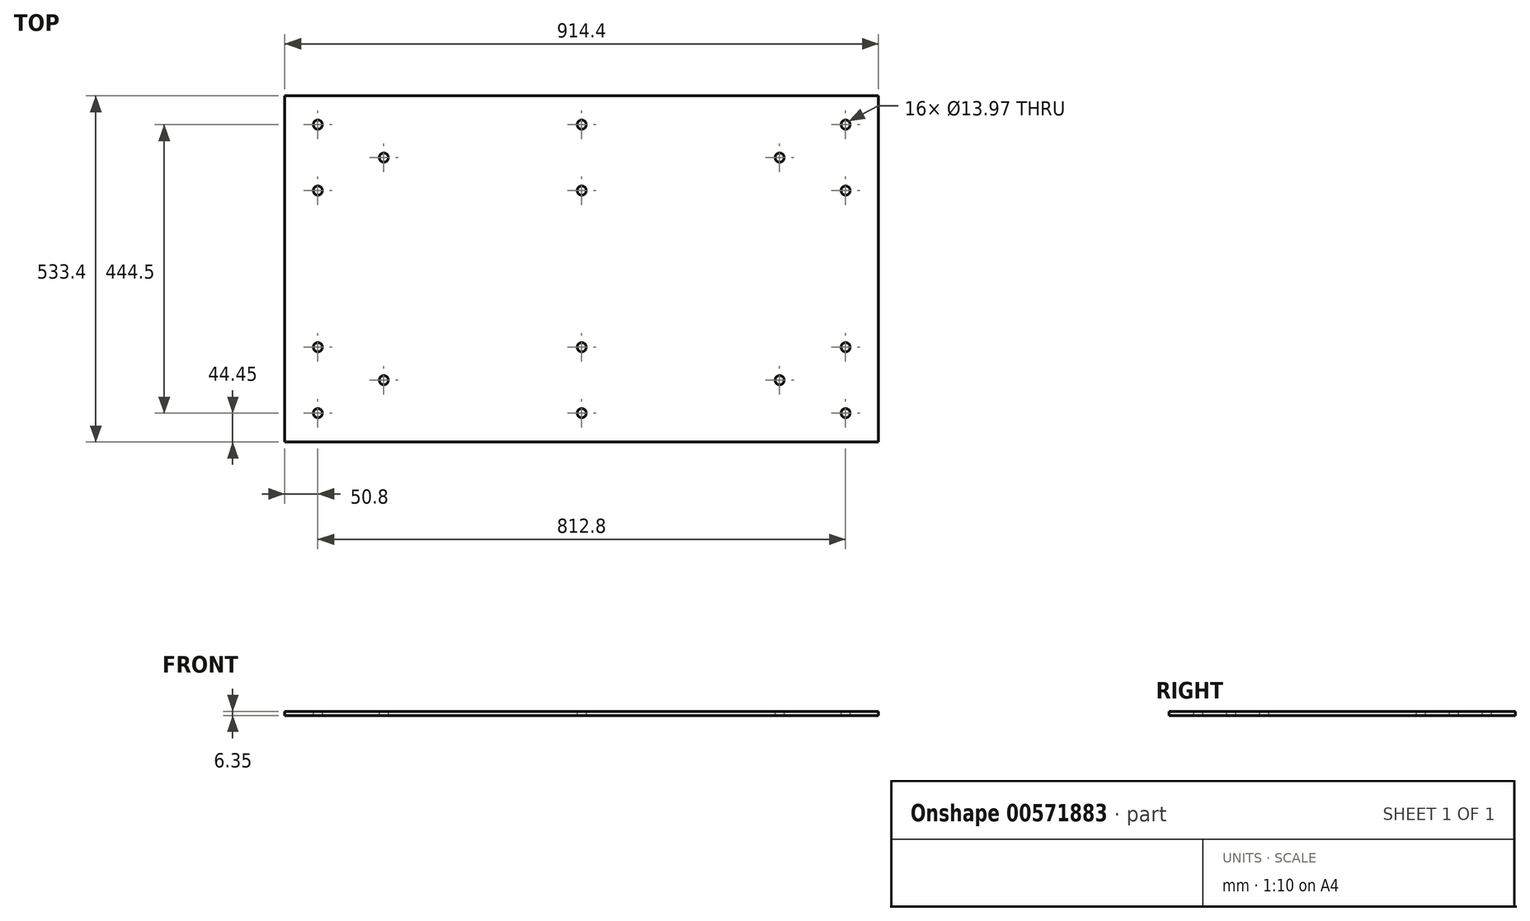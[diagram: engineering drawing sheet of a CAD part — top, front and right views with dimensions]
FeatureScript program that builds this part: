
annotation { "Feature Type Name" : "Feature", "Feature Type Description" : "" }
export const myFeature = defineFeature(function(context is Context, id is Id, definition is map)
    precondition{}
    {
        {
            var Q0;
            Q0=qCreatedBy(makeId("Top.planeOp"),FACE);
            var sketch = newSketch(context, id + "F0", { "sketchPlane" : qUnion([Q0])});
            skLineSegment(sketch, "E0", {"start": v(0, 266.7) * mm, "end": v(0, -266.7) * mm});
            skLineSegment(sketch, "E1", {"start": v(0, 266.7) * mm, "end": v(914.4, 266.7) * mm});
            skLineSegment(sketch, "E2", {"start": v(914.4, 266.7) * mm, "end": v(914.4, -266.7) * mm});
            skLineSegment(sketch, "E3", {"start": v(914.4, -266.7) * mm, "end": v(0, -266.7) * mm});
            skLineSegment(sketch, "E4", {"start": v(0, 82.55) * mm, "end": v(914.4, 82.55) * mm});
            skLineSegment(sketch, "E5", {"start": v(0, -82.55) * mm, "end": v(914.4, -82.55) * mm});
            skCircle(sketch, "E6", {"center": v(50.8, 222.25) * mm, "radius": 6.99 * mm});
            skCircle(sketch, "E7", {"center": v(152.4, 171.45) * mm, "radius": 6.99 * mm});
            skCircle(sketch, "E8", {"center": v(457.2, 222.25) * mm, "radius": 6.99 * mm});
            skLineSegment(sketch, "E9", {"start": v(457.2, 266.7) * mm, "end": v(457.2, -266.7) * mm, "construction": true});
            skLineSegment(sketch, "E10", {"start": v(0, 171.45) * mm, "end": v(914.4, 171.45) * mm, "construction": true});
            skCircle(sketch, "E11.MirrorC", {"center": v(50.8, 120.65) * mm, "radius": 6.99 * mm});
            skCircle(sketch, "E12.MirrorC", {"center": v(762, 171.45) * mm, "radius": 6.99 * mm});
            skCircle(sketch, "E13.MirrorC", {"center": v(863.6, 222.25) * mm, "radius": 6.99 * mm});
            skCircle(sketch, "E14.MirrorC", {"center": v(863.6, 120.65) * mm, "radius": 6.99 * mm});
            skLineSegment(sketch, "E15", {"start": v(0, 0) * mm, "end": v(914.4, 0) * mm, "construction": true});
            skCircle(sketch, "E16.MirrorC", {"center": v(50.8, -222.25) * mm, "radius": 6.99 * mm});
            skCircle(sketch, "E17.MirrorC", {"center": v(50.8, -120.65) * mm, "radius": 6.99 * mm});
            skCircle(sketch, "E18.MirrorC", {"center": v(152.4, -171.45) * mm, "radius": 6.99 * mm});
            skCircle(sketch, "E19.MirrorC", {"center": v(762, -171.45) * mm, "radius": 6.99 * mm});
            skCircle(sketch, "E20.MirrorC", {"center": v(863.6, -222.25) * mm, "radius": 6.99 * mm});
            skCircle(sketch, "E21.MirrorC", {"center": v(863.6, -120.65) * mm, "radius": 6.99 * mm});
            skCircle(sketch, "E22.MirrorC", {"center": v(457.2, -222.25) * mm, "radius": 6.99 * mm});
            skCircle(sketch, "E23.MirrorC", {"center": v(457.2, 120.65) * mm, "radius": 6.99 * mm});
            skCircle(sketch, "E24.MirrorC", {"center": v(457.2, -120.65) * mm, "radius": 6.99 * mm});
            skSolve(sketch);
        }
        {
            var Q0;
            Q0 = qSketchRegion(id + "F0", true);
            extrude(context, id + "F1", {"entities" : qUnion([Q0]), "depth" : 6.35 * mm, "offsetDistance" : 25.4 * mm});
        }
    });
